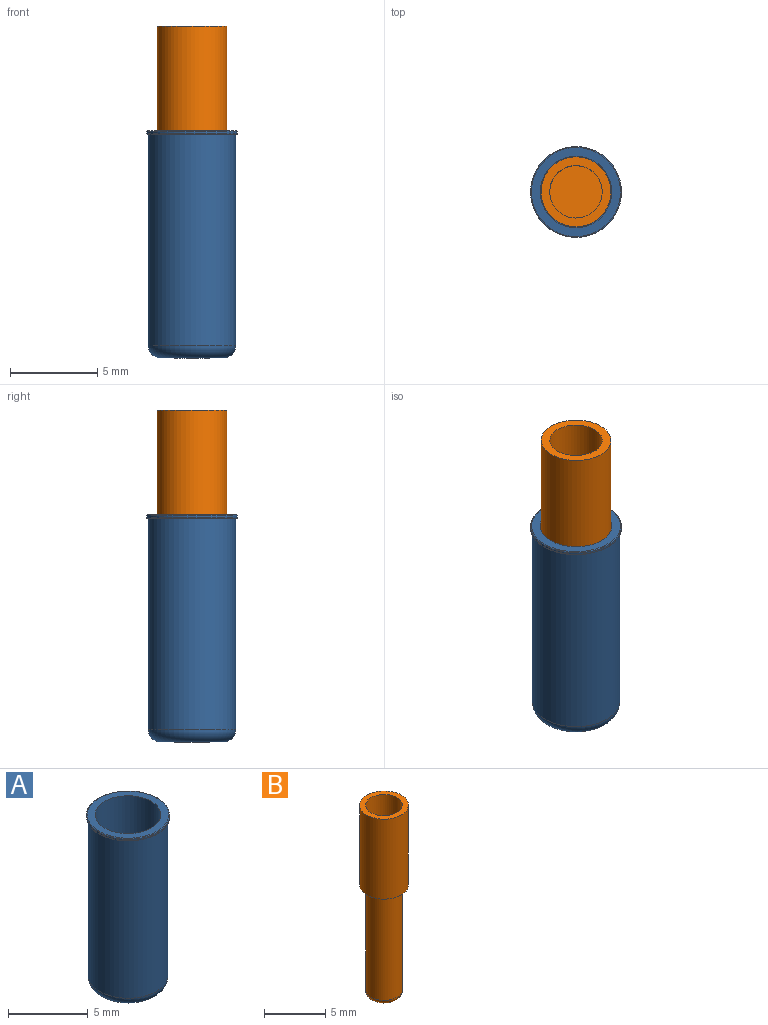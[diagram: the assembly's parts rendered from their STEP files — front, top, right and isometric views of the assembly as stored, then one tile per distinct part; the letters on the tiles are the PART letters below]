
ASSEMBLY  parts=2 mates=1
PART A: 11 faces, bbox 5.6x5.6x13 mm
  f0: cylinder r=2.5mm len=12.1mm, axis (0,0,1), area 190.1mm2, adj f4,f8
  f1: plane 3.6x3.6mm, normal (0,0,-1), area 3.1mm2, adj f7,f8
  f2: cylinder r=2.6mm len=5.2mm, axis (0,0,-1), area 1.6mm2, adj f9,f10
  f3: plane 5.1x5.1mm, normal (0,0,1), area 7.2mm2, adj f5,f10
  f4: plane 5.1x5.1mm, normal (0,0,-1), area 0.8mm2, adj f0,f9
  f5: cylinder r=2.05mm len=8mm, axis (0,0,1), area 103mm2, adj f3,f6
  f6: plane 4.1x4.1mm, normal (0,0,1), area 6.1mm2, adj f5,f7
  f7: cylinder r=1.5mm len=5mm, axis (0,0,1), area 47.1mm2, adj f1,f6
  f8: torus R=1.8mm, axis (0,0,1), area 15.5mm2, adj f0,f1
  f9: torus R=2.55mm, axis (0,0,1), area 1.3mm2, adj f2,f4
  f10: torus R=2.55mm, axis (0,0,1), area 1.3mm2, adj f2,f3
PART B: 8 faces, bbox 4x4x19 mm
  f0: cylinder r=1.5mm len=6mm, axis (0,0,-1), area 56.5mm2, adj f2,f3
  f1: cylinder r=2mm len=8mm, axis (0,0,-1), area 100.5mm2, adj f2,f4
  f2: plane 4x4mm, normal (0,0,1), area 5.5mm2, adj f0,f1
  f3: plane 3x3mm, normal (0,0,1), area 7.1mm2, adj f0
  f4: plane 4x4mm, normal (0,0,-1), area 5.5mm2, adj f1,f5
  f5: cylinder r=1.5mm len=10.5mm, axis (0,0,1), area 99mm2, adj f4,f7
  f6: plane 2x2mm, normal (0,0,-1), area 3.1mm2, adj f7
  f7: torus R=1mm, axis (0,0,-1), area 6.5mm2, adj f5,f6
PLACE A t=(-8.6,-6.62,20.97)mm
PLACE B t=(-8.6,-6.62,21.17)mm
MATE slider B.f5 <-> A.f7  axis (0,0,1) through (-8.6,-6.62,13.92)mm
